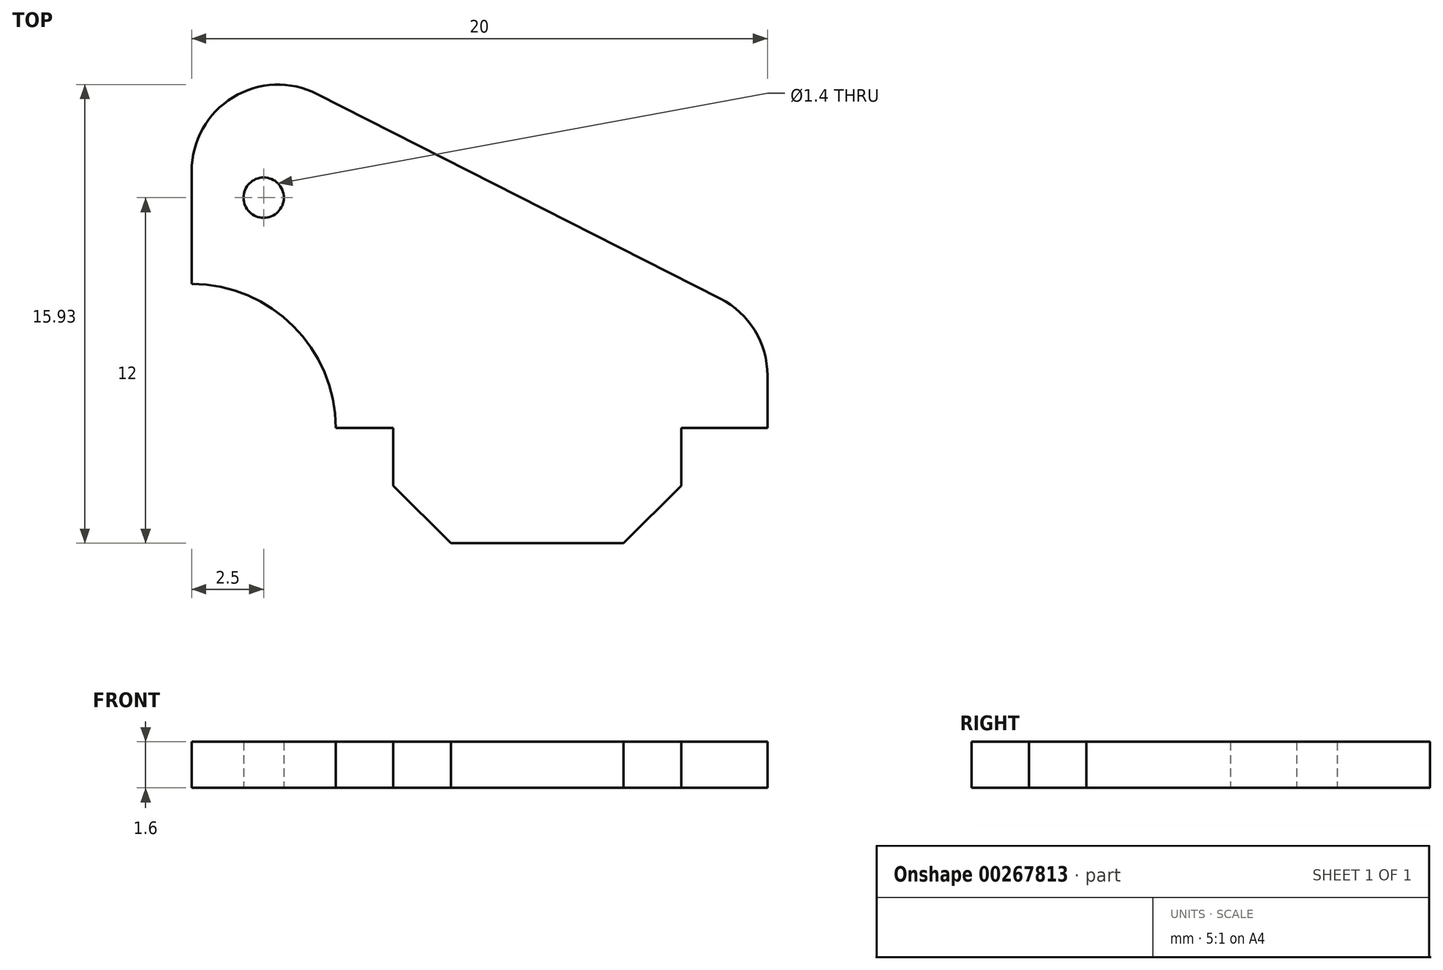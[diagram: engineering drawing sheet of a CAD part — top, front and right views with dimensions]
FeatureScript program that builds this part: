
annotation { "Feature Type Name" : "Feature", "Feature Type Description" : "" }
export const myFeature = defineFeature(function(context is Context, id is Id, definition is map)
    precondition{}
    {
        {
            var Q0;
            Q0=qCreatedBy(makeId("Top.planeOp"),FACE);
            var sketch = newSketch(context, id + "F0", { "sketchPlane" : qUnion([Q0])});
            skLineSegment(sketch, "E0", {"start": v(0, 61.58) * mm, "end": v(0, -73.73) * mm, "construction": true});
            skLineSegment(sketch, "E1", {"start": v(-53.77, 0) * mm, "end": v(91.4, 0) * mm, "construction": true});
            skLineSegment(sketch, "E2", {"start": v(-2.5, -3) * mm, "end": v(-2.5, 0.93) * mm});
            skLineSegment(sketch, "E3.0", {"start": v(2.5, -8) * mm, "end": v(4.5, -8) * mm});
            skLineSegment(sketch, "E4", {"start": v(17.5, -8) * mm, "end": v(17.5, -6.18) * mm});
            skLineSegment(sketch, "E5", {"start": v(4.5, -10) * mm, "end": v(4.5, -8) * mm});
            skLineSegment(sketch, "E6", {"start": v(14.5, -10) * mm, "end": v(14.5, -8) * mm});
            skLineSegment(sketch, "E7", {"start": v(15.86, -3.5) * mm, "end": v(1.86, 3.6) * mm});
            skLineSegment(sketch, "E8.trimOffspring", {"start": v(6.5, -12) * mm, "end": v(12.5, -12) * mm});
            skLineSegment(sketch, "E9.trimOffspring", {"start": v(14.5, -8) * mm, "end": v(17.5, -8) * mm});
            skCircle(sketch, "E10", {"center": v(0, 0) * mm, "radius": 0.7 * mm});
            skPoint(sketch, "E11", {"position": v(2.5, -8) * mm});
            skArc(sketch, "E12", {"start": v(2.5, -8) * mm, "mid": v(1.04, -4.46) * mm, "end": v(-2.5, -3) * mm});
            skPoint(sketch, "E13.visualSharp", {"position": v(-2.5, 5.81) * mm});
            skArc(sketch, "E13.filletArc", {"start": v(1.86, 3.6) * mm, "mid": v(-1.07, 3.48) * mm, "end": v(-2.5, 0.93) * mm});
            skPoint(sketch, "E14.visualSharp", {"position": v(17.5, -4.34) * mm});
            skArc(sketch, "E14.filletArc", {"start": v(17.5, -6.18) * mm, "mid": v(17.06, -4.61) * mm, "end": v(15.86, -3.5) * mm});
            skPoint(sketch, "E15", {"position": v(4.5, -10) * mm});
            skPoint(sketch, "E16", {"position": v(14.5, -10) * mm});
            skPoint(sketch, "E17", {"position": v(6.5, -12) * mm});
            skPoint(sketch, "E18", {"position": v(12.5, -12) * mm});
            skLineSegment(sketch, "E19", {"start": v(4.5, -10) * mm, "end": v(6.5, -12) * mm});
            skLineSegment(sketch, "E20", {"start": v(12.5, -12) * mm, "end": v(14.5, -10) * mm});
            skPoint(sketch, "E21.orphan", {"position": v(4.5, -12) * mm});
            skPoint(sketch, "E22.orphan", {"position": v(14.5, -12) * mm});
            skSolve(sketch);
        }
        {
            var Q0;
            Q0=makeQuery(id+"F0.imprint","IMPRINT",FACE,{"disambiguationData":[TD([[makeQuery(id+"F0.imprint","IMPRINT",EDGE,{"derivedFrom":sQuery(id+"F0.wireOp",EDGE,"E2")}),-1.0]])]});
            extrude(context, id + "F1", {"entities" : qUnion([Q0]), "depth" : 1.6 * mm});
        }
    });
